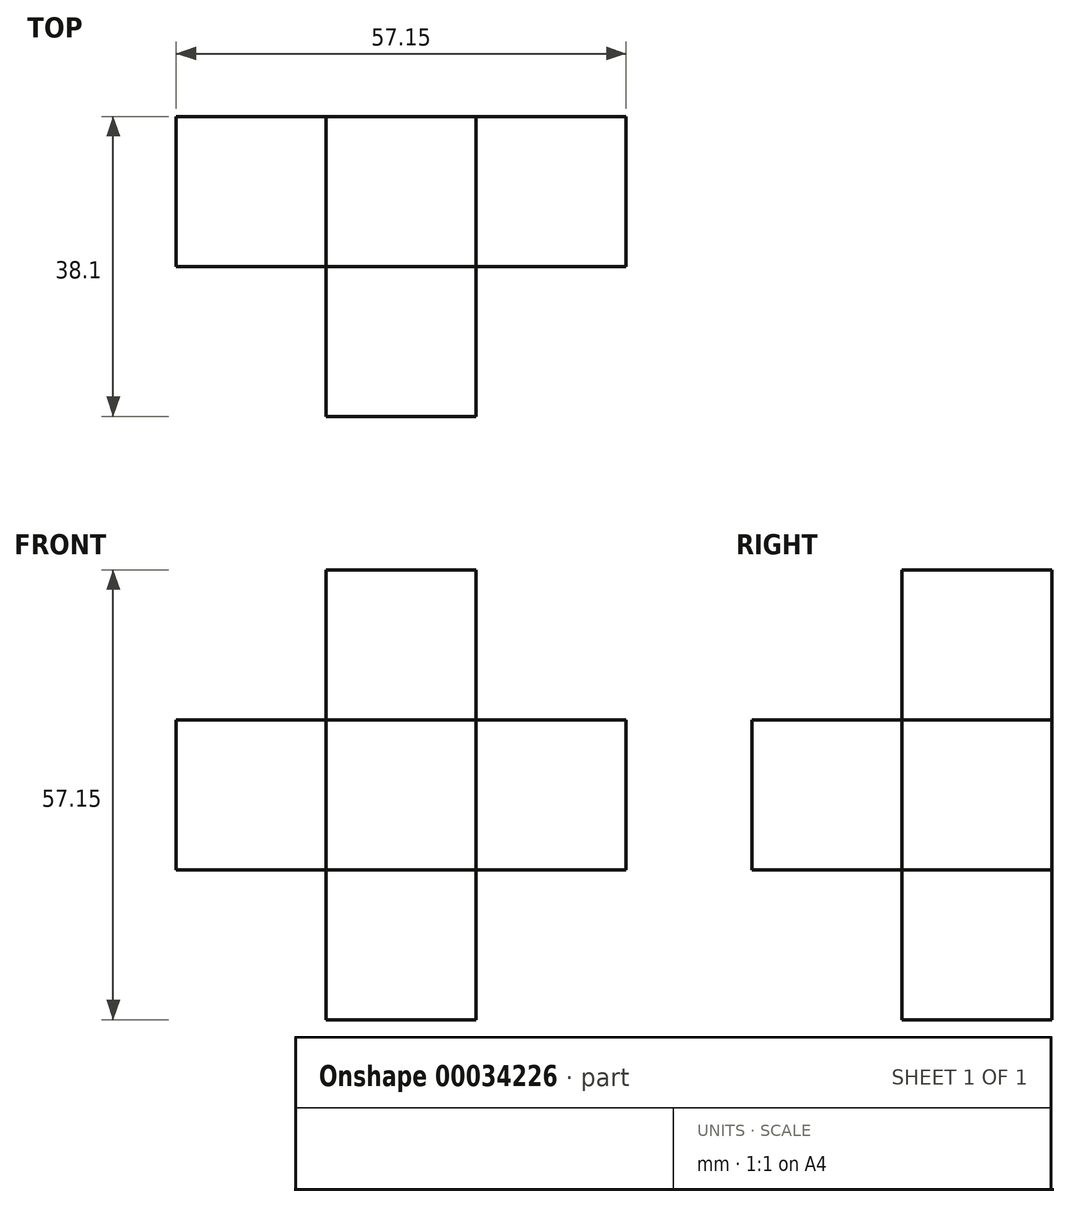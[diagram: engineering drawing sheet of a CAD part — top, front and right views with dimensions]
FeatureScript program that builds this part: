
annotation { "Feature Type Name" : "Feature", "Feature Type Description" : "" }
export const myFeature = defineFeature(function(context is Context, id is Id, definition is map)
    precondition{}
    {
        {
            var Q0;
            Q0=qCreatedBy(makeId("Top.planeOp"),FACE);
            var sketch = newSketch(context, id + "F0", { "sketchPlane" : qUnion([Q0])});
            skLineSegment(sketch, "E0.bottom", {"start": v(0, 0) * mm, "end": v(19.05, 0) * mm});
            skLineSegment(sketch, "E0.top", {"start": v(0, -19.05) * mm, "end": v(19.05, -19.05) * mm});
            skLineSegment(sketch, "E0.left", {"start": v(0, 0) * mm, "end": v(0, -19.05) * mm});
            skLineSegment(sketch, "E0.right", {"start": v(19.05, 0) * mm, "end": v(19.05, -19.05) * mm});
            skSolve(sketch);
        }
        {
            var Q0;
            Q0 = qSketchRegion(id + "F0", true);
            extrude(context, id + "F1", {"entities" : qUnion([Q0]), "depth" : 57.15 * mm});
        }
        {
            var Q0;
            Q0=qCreatedBy(makeId("Front.planeOp"),FACE);
            var sketch = newSketch(context, id + "F2", { "sketchPlane" : qUnion([Q0])});
            skLineSegment(sketch, "E1.bottom", {"start": v(0, 38.1) * mm, "end": v(19.05, 38.1) * mm});
            skLineSegment(sketch, "E1.top", {"start": v(0, 19.05) * mm, "end": v(19.05, 19.05) * mm});
            skLineSegment(sketch, "E1.left", {"start": v(0, 38.1) * mm, "end": v(0, 19.05) * mm});
            skLineSegment(sketch, "E1.right", {"start": v(19.05, 38.1) * mm, "end": v(19.05, 19.05) * mm});
            skSolve(sketch);
        }
        {
            var Q0;
            Q0=qCreatedBy(makeId("Front.planeOp"),FACE);
            var sketch = newSketch(context, id + "F3", { "sketchPlane" : qUnion([Q0])});
            skLineSegment(sketch, "E2.bottom", {"start": v(0, 38.1) * mm, "end": v(19.05, 38.1) * mm});
            skLineSegment(sketch, "E2.top", {"start": v(0, 19.05) * mm, "end": v(19.05, 19.05) * mm});
            skLineSegment(sketch, "E2.left", {"start": v(0, 38.1) * mm, "end": v(0, 19.05) * mm});
            skLineSegment(sketch, "E2.right", {"start": v(19.05, 38.1) * mm, "end": v(19.05, 19.05) * mm});
            skSolve(sketch);
        }
        {
            var Q0;
            Q0=qCreatedBy(makeId("Right.planeOp"),FACE);
            var sketch = newSketch(context, id + "F4", { "sketchPlane" : qUnion([Q0])});
            skLineSegment(sketch, "E3.bottom", {"start": v(0, 38.1) * mm, "end": v(-19.05, 38.1) * mm});
            skLineSegment(sketch, "E3.top", {"start": v(0, 19.05) * mm, "end": v(-19.05, 19.05) * mm});
            skLineSegment(sketch, "E3.left", {"start": v(0, 38.1) * mm, "end": v(0, 19.05) * mm});
            skLineSegment(sketch, "E3.right", {"start": v(-19.05, 38.1) * mm, "end": v(-19.05, 19.05) * mm});
            skSolve(sketch);
        }
        {
            var Q0;
            Q0 = qSketchRegion(id + "F4", true);
            extrude(context, id + "F5", {"entities" : qUnion([Q0]), "operationType" : NewBodyOperationType.ADD, "oppositeDirection" : true, "depth" : 19.05 * mm});
        }
        {
            var Q0;
            Q0 = qSketchRegion(id + "F4", true);
            extrude(context, id + "F6", {"entities" : qUnion([Q0]), "operationType" : NewBodyOperationType.ADD, "depth" : 38.1 * mm});
        }
        {
            var Q0;
            Q0=makeQuery(id+"F2.imprint","IMPRINT",FACE,{"disambiguationData":[TD([[makeQuery(id+"F2.imprint","IMPRINT",EDGE,{"derivedFrom":sQuery(id+"F2.wireOp",EDGE,"E1.bottom")}),-1.0]])]});
            extrude(context, id + "F7", {"entities" : qUnion([Q0]), "operationType" : NewBodyOperationType.ADD, "depth" : 38.1 * mm});
        }
    });
